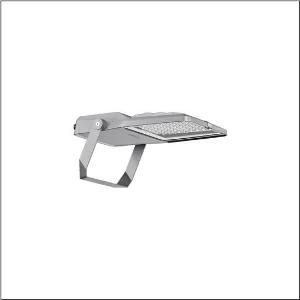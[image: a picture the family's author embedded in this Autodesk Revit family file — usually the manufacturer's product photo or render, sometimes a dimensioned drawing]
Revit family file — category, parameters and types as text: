
# Revit family: floodlight_fl_21_mini___pl43_5xa7776c2a1a_c133
name_source: partatom
category: Lighting Fixtures
units: mm (PartAtom-declared; Revit-internal decimal feet)

## family parameters
Cut with Voids When Loaded = No
Host = Face
Light Source = No
Part Type = Normal
Room Calculation Point = No
Round Connector Dimension = Use Diameter
Shared = No

## types (1)
- --- (1 x LED, 12500 lm, 89 W, 3000K)
    Apparent Load = 89 VA
    CIE Flux Codes = 27 78 99 100 100
    Color Rendering = 70
    Color Temperature = 3000K
    Default Elevation = 1800 mm
    Description = Floodlight FL 21 mini, floodlight, primary light control with lens, of PMMA, primary optical cover: protective disc, of toughened safety glass, transparent, light distribution: PL43, light emission: direct distribution, installation type: surface-mounted, LED, High Power LED, rated luminous flux: 12.500lm, luminous efficacy: 140lm/W, light colour: 730, colour temperature: 3000K, control: flexible luminous flux parameterisation, time-dependent luminous flux control, constant luminous flux control, overheat protection, presetting dimming logarithmic, with terminal, 6-pole, mains connection: 220..240V, AC, 50/60Hz, start of lifetime: 89W, end of service life: 94W, reduction: 43W, luminaire housing, of diecast aluminium, powder-coated, Siteco® metallic grey (DB 702S), corrosivity category C5 mid according to DIN EN ISO 12944, sealing non-destructively replaceable, mounting bracket, of steel, galvanised, powder-coated, Siteco® metallic grey (DB 702S), Smart Interface below and above, protection rating (complete): IP66, insulation class (complete): insulation class II (safety insulation), certification: CE, ENEC, VDE, protection symbol: D, impact resistance: IK08, permissible operating ambient temperature: -40..+40°C, permissible operating ambient temperature for outdoor applications: -40..+50°C, standard: DIN EN 12944, LABS conformity tested according to VDMA 24364:2018-05, packaging unit: 1 piece

Light Distribution: PL43
    Height = 70 mm
    Lamp = 1 x LED
    Lamp Light Flux = 12500 lm
    Lamp Power = 89 W
    Lamp count = 1
    Length = 485 mm
    Luminous efficacy = 140 lm/W
    Manufacturer = Siteco
    ModVariant = No
    Model = 5XA7776C2A1A
    Number of Poles = 1
    OnlyDefault = Yes
    Power Factor = 1
    Product Name = Floodlight FL 21 mini | PL43
    Product group = floodlight | pylon annexe
    ProductGroupID = 6200
    Protection Class = Protection class II
    Protection Degree = IP 66
    RLX_Detail_Level = 1
    RLX_Emergency_Light_Flux = 0 lm
    RLX_Emergency_Type = 0
    RLX_Emergency_Type_DB = No
    RlxData = <blob elided: 95725 chars, md5=d435b609>
    Socket = socket
    Standby Power = 0 W
    System Light Flux = 12500 lm
    System Power = 89 W
    Type Comments = factory setting: luminous flux: 100 % | dim-lin: 254 | 456 mA
    Type Image = l_1006845.jpg
    URL = http://relux.com
    VarID = @adj_093459
    Voltage = 0 V
    Weight = 0.00 kg
    Width = 337 mm

## geometry (parser evidence)
native form markers: Blend x4, Sweep x11
no freeform markers — native parametric forms only
